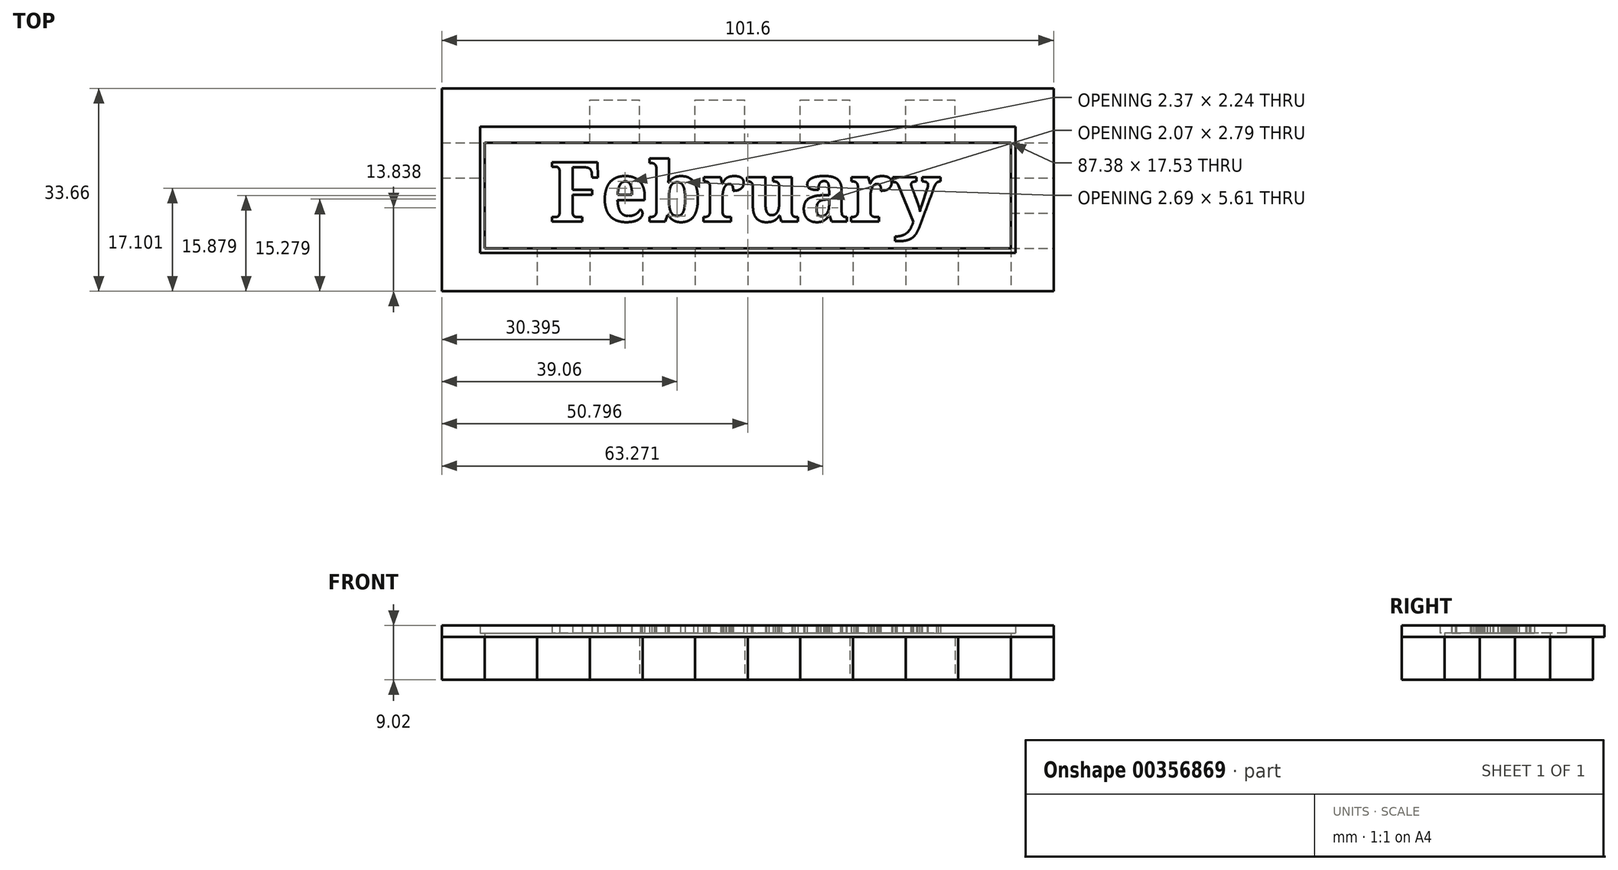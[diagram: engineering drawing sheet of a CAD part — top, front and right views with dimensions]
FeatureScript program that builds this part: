
annotation { "Feature Type Name" : "Feature", "Feature Type Description" : "" }
export const myFeature = defineFeature(function(context is Context, id is Id, definition is map)
    precondition{}
    {
        {
            var Q0;
            Q0=qCreatedBy(makeId("Top.planeOp"),FACE);
            var sketch = newSketch(context, id + "F0", { "sketchPlane" : qUnion([Q0])});
            skLineSegment(sketch, "E0.bottom", {"start": v(-52.12, 11.37) * mm, "end": v(49.48, 11.37) * mm});
            skLineSegment(sketch, "E0.top", {"start": v(-52.12, -20.38) * mm, "end": v(49.48, -20.38) * mm});
            skLineSegment(sketch, "E0.left", {"start": v(-52.12, 11.37) * mm, "end": v(-52.12, -20.38) * mm});
            skLineSegment(sketch, "E0.right", {"start": v(49.48, 11.37) * mm, "end": v(49.48, -20.38) * mm});
            skLineSegment(sketch, "E1.bottom", {"start": v(-52.12, 11.37) * mm, "end": v(-45.01, 11.37) * mm});
            skLineSegment(sketch, "E1.top", {"start": v(-52.12, 4.26) * mm, "end": v(-45.01, 4.26) * mm});
            skLineSegment(sketch, "E1.left", {"start": v(-52.12, 11.37) * mm, "end": v(-52.12, 4.26) * mm});
            skLineSegment(sketch, "E1.right", {"start": v(-45.01, 11.37) * mm, "end": v(-45.01, 4.26) * mm});
            skLineSegment(sketch, "E2.bottom", {"start": v(-45.01, 11.37) * mm, "end": v(-36.78, 11.37) * mm});
            skLineSegment(sketch, "E2.top", {"start": v(-45.01, 4.26) * mm, "end": v(-36.78, 4.26) * mm});
            skLineSegment(sketch, "E2.right", {"start": v(-36.78, 11.37) * mm, "end": v(-36.78, 4.26) * mm});
            skLineSegment(sketch, "E3.bottom", {"start": v(-36.78, 4.26) * mm, "end": v(-27.54, 4.26) * mm});
            skLineSegment(sketch, "E3.top", {"start": v(-36.78, 11.37) * mm, "end": v(-27.54, 11.37) * mm});
            skLineSegment(sketch, "E3.left", {"start": v(-36.78, 4.26) * mm, "end": v(-36.78, 11.37) * mm});
            skLineSegment(sketch, "E3.right", {"start": v(-27.54, 4.26) * mm, "end": v(-27.54, 11.37) * mm});
            skLineSegment(sketch, "E4.bottom", {"start": v(-27.54, 4.26) * mm, "end": v(-19.3, 4.26) * mm});
            skLineSegment(sketch, "E4.top", {"start": v(-27.54, 11.37) * mm, "end": v(-19.3, 11.37) * mm});
            skLineSegment(sketch, "E4.right", {"start": v(-19.3, 4.26) * mm, "end": v(-19.3, 11.37) * mm});
            skLineSegment(sketch, "E5.bottom", {"start": v(-19.3, 4.26) * mm, "end": v(-10.06, 4.26) * mm});
            skLineSegment(sketch, "E5.top", {"start": v(-19.3, 11.37) * mm, "end": v(-10.06, 11.37) * mm});
            skLineSegment(sketch, "E5.right", {"start": v(-10.06, 4.26) * mm, "end": v(-10.06, 11.37) * mm});
            skLineSegment(sketch, "E6.bottom", {"start": v(-10.06, 4.26) * mm, "end": v(-10.06, 4.26) * mm});
            skLineSegment(sketch, "E6.top", {"start": v(-10.06, 11.37) * mm, "end": v(-10.06, 11.37) * mm});
            skLineSegment(sketch, "E7.bottom", {"start": v(-10.06, 4.26) * mm, "end": v(-1.83, 4.26) * mm});
            skLineSegment(sketch, "E7.top", {"start": v(-10.06, 11.37) * mm, "end": v(-1.83, 11.37) * mm});
            skLineSegment(sketch, "E7.right", {"start": v(-1.83, 4.26) * mm, "end": v(-1.83, 11.37) * mm});
            skLineSegment(sketch, "E8.bottom", {"start": v(-1.83, 4.26) * mm, "end": v(7.41, 4.26) * mm});
            skLineSegment(sketch, "E8.top", {"start": v(-1.83, 11.37) * mm, "end": v(7.41, 11.37) * mm});
            skLineSegment(sketch, "E8.right", {"start": v(7.41, 4.26) * mm, "end": v(7.41, 11.37) * mm});
            skLineSegment(sketch, "E9.bottom", {"start": v(7.41, 4.26) * mm, "end": v(15.64, 4.26) * mm});
            skLineSegment(sketch, "E9.top", {"start": v(7.41, 11.37) * mm, "end": v(15.64, 11.37) * mm});
            skLineSegment(sketch, "E9.right", {"start": v(15.64, 4.26) * mm, "end": v(15.64, 11.37) * mm});
            skLineSegment(sketch, "E10.bottom", {"start": v(15.64, 4.26) * mm, "end": v(24.89, 4.26) * mm});
            skLineSegment(sketch, "E10.top", {"start": v(15.64, 11.37) * mm, "end": v(24.89, 11.37) * mm});
            skLineSegment(sketch, "E10.right", {"start": v(24.89, 4.26) * mm, "end": v(24.89, 11.37) * mm});
            skLineSegment(sketch, "E11.bottom", {"start": v(24.89, 4.26) * mm, "end": v(24.89, 4.26) * mm});
            skLineSegment(sketch, "E11.top", {"start": v(24.89, 11.37) * mm, "end": v(24.89, 11.37) * mm});
            skLineSegment(sketch, "E12.bottom", {"start": v(24.89, 4.26) * mm, "end": v(33.12, 4.26) * mm});
            skLineSegment(sketch, "E12.top", {"start": v(24.89, 11.37) * mm, "end": v(33.12, 11.37) * mm});
            skLineSegment(sketch, "E12.right", {"start": v(33.12, 4.26) * mm, "end": v(33.12, 11.37) * mm});
            skLineSegment(sketch, "E13.bottom", {"start": v(33.12, 4.26) * mm, "end": v(42.36, 4.26) * mm});
            skLineSegment(sketch, "E13.top", {"start": v(33.12, 11.37) * mm, "end": v(42.36, 11.37) * mm});
            skLineSegment(sketch, "E13.right", {"start": v(42.36, 4.26) * mm, "end": v(42.36, 11.37) * mm});
            skLineSegment(sketch, "E14.bottom", {"start": v(42.36, 4.26) * mm, "end": v(49.48, 4.26) * mm});
            skLineSegment(sketch, "E14.top", {"start": v(42.36, 11.37) * mm, "end": v(49.48, 11.37) * mm});
            skLineSegment(sketch, "E14.right", {"start": v(49.48, 4.26) * mm, "end": v(49.48, 11.37) * mm});
            skLineSegment(sketch, "E15.bottom", {"start": v(-52.12, -20.38) * mm, "end": v(-45.01, -20.38) * mm});
            skLineSegment(sketch, "E15.top", {"start": v(-52.12, -13.26) * mm, "end": v(-45.01, -13.26) * mm});
            skLineSegment(sketch, "E15.left", {"start": v(-52.12, -20.38) * mm, "end": v(-52.12, -13.26) * mm});
            skLineSegment(sketch, "E15.right", {"start": v(-45.01, -20.38) * mm, "end": v(-45.01, -13.26) * mm});
            skLineSegment(sketch, "E16.bottom", {"start": v(-45.01, -13.26) * mm, "end": v(-45.01, -13.26) * mm});
            skLineSegment(sketch, "E16.top", {"start": v(-45.01, -20.38) * mm, "end": v(-45.01, -20.38) * mm});
            skLineSegment(sketch, "E16.left", {"start": v(-45.01, -13.26) * mm, "end": v(-45.01, -20.38) * mm});
            skLineSegment(sketch, "E16.right", {"start": v(-45.01, -13.26) * mm, "end": v(-45.01, -20.38) * mm});
            skLineSegment(sketch, "E17.bottom", {"start": v(-45.01, -13.26) * mm, "end": v(-36.27, -13.26) * mm});
            skLineSegment(sketch, "E17.top", {"start": v(-45.01, -20.38) * mm, "end": v(-36.27, -20.38) * mm});
            skLineSegment(sketch, "E17.right", {"start": v(-36.27, -13.26) * mm, "end": v(-36.27, -20.38) * mm});
            skLineSegment(sketch, "E18.bottom", {"start": v(-36.27, -13.26) * mm, "end": v(-36.27, -13.26) * mm});
            skLineSegment(sketch, "E18.top", {"start": v(-36.27, -20.38) * mm, "end": v(-36.27, -20.38) * mm});
            skLineSegment(sketch, "E19.bottom", {"start": v(-36.27, -13.26) * mm, "end": v(-27.54, -13.26) * mm});
            skLineSegment(sketch, "E19.top", {"start": v(-36.27, -20.38) * mm, "end": v(-27.54, -20.38) * mm});
            skLineSegment(sketch, "E19.right", {"start": v(-27.54, -13.26) * mm, "end": v(-27.54, -20.38) * mm});
            skLineSegment(sketch, "E20.bottom", {"start": v(-27.54, -13.26) * mm, "end": v(-18.8, -13.26) * mm});
            skLineSegment(sketch, "E20.top", {"start": v(-27.54, -20.38) * mm, "end": v(-18.8, -20.38) * mm});
            skLineSegment(sketch, "E20.right", {"start": v(-18.8, -13.26) * mm, "end": v(-18.8, -20.38) * mm});
            skLineSegment(sketch, "E21.bottom", {"start": v(-18.8, -13.26) * mm, "end": v(-10.06, -13.26) * mm});
            skLineSegment(sketch, "E21.top", {"start": v(-18.8, -20.38) * mm, "end": v(-10.06, -20.38) * mm});
            skLineSegment(sketch, "E21.right", {"start": v(-10.06, -13.26) * mm, "end": v(-10.06, -20.38) * mm});
            skLineSegment(sketch, "E22.bottom", {"start": v(-10.06, -13.26) * mm, "end": v(-1.32, -13.26) * mm});
            skLineSegment(sketch, "E22.top", {"start": v(-10.06, -20.38) * mm, "end": v(-1.32, -20.38) * mm});
            skLineSegment(sketch, "E22.right", {"start": v(-1.32, -13.26) * mm, "end": v(-1.32, -20.38) * mm});
            skLineSegment(sketch, "E23.bottom", {"start": v(-1.32, -13.26) * mm, "end": v(7.41, -13.26) * mm});
            skLineSegment(sketch, "E23.top", {"start": v(-1.32, -20.38) * mm, "end": v(7.41, -20.38) * mm});
            skLineSegment(sketch, "E23.right", {"start": v(7.41, -13.26) * mm, "end": v(7.41, -20.38) * mm});
            skLineSegment(sketch, "E24.bottom", {"start": v(7.41, -13.26) * mm, "end": v(16.15, -13.26) * mm});
            skLineSegment(sketch, "E24.top", {"start": v(7.41, -20.38) * mm, "end": v(16.15, -20.38) * mm});
            skLineSegment(sketch, "E24.right", {"start": v(16.15, -13.26) * mm, "end": v(16.15, -20.38) * mm});
            skLineSegment(sketch, "E25.bottom", {"start": v(16.15, -13.26) * mm, "end": v(24.89, -13.26) * mm});
            skLineSegment(sketch, "E25.top", {"start": v(16.15, -20.38) * mm, "end": v(24.89, -20.38) * mm});
            skLineSegment(sketch, "E25.right", {"start": v(24.89, -13.26) * mm, "end": v(24.89, -20.38) * mm});
            skLineSegment(sketch, "E26.bottom", {"start": v(24.89, -13.26) * mm, "end": v(33.63, -13.26) * mm});
            skLineSegment(sketch, "E26.top", {"start": v(24.89, -20.38) * mm, "end": v(33.63, -20.38) * mm});
            skLineSegment(sketch, "E26.right", {"start": v(33.63, -13.26) * mm, "end": v(33.63, -20.38) * mm});
            skLineSegment(sketch, "E27.bottom", {"start": v(33.63, -13.26) * mm, "end": v(42.36, -13.26) * mm});
            skLineSegment(sketch, "E27.top", {"start": v(33.63, -20.38) * mm, "end": v(42.36, -20.38) * mm});
            skLineSegment(sketch, "E27.right", {"start": v(42.36, -13.26) * mm, "end": v(42.36, -20.38) * mm});
            skLineSegment(sketch, "E28.bottom", {"start": v(42.36, -13.26) * mm, "end": v(49.48, -13.26) * mm});
            skLineSegment(sketch, "E28.top", {"start": v(42.36, -20.38) * mm, "end": v(49.48, -20.38) * mm});
            skLineSegment(sketch, "E28.right", {"start": v(49.48, -13.26) * mm, "end": v(49.48, -20.38) * mm});
            skLineSegment(sketch, "E29.top", {"start": v(-52.12, -1.58) * mm, "end": v(-45.01, -1.58) * mm});
            skLineSegment(sketch, "E29.left", {"start": v(-52.12, 4.26) * mm, "end": v(-52.12, -1.58) * mm});
            skLineSegment(sketch, "E29.right", {"start": v(-45.01, 4.26) * mm, "end": v(-45.01, -1.58) * mm});
            skLineSegment(sketch, "E30.top", {"start": v(-52.12, -7.42) * mm, "end": v(-45.01, -7.42) * mm});
            skLineSegment(sketch, "E30.left", {"start": v(-52.12, -1.58) * mm, "end": v(-52.12, -7.42) * mm});
            skLineSegment(sketch, "E30.right", {"start": v(-45.01, -1.58) * mm, "end": v(-45.01, -7.42) * mm});
            skLineSegment(sketch, "E31.bottom", {"start": v(-45.01, -7.42) * mm, "end": v(-52.12, -7.42) * mm});
            skLineSegment(sketch, "E31.top", {"start": v(-45.01, -13.26) * mm, "end": v(-52.12, -13.26) * mm});
            skLineSegment(sketch, "E31.left", {"start": v(-45.01, -7.42) * mm, "end": v(-45.01, -13.26) * mm});
            skLineSegment(sketch, "E31.right", {"start": v(-52.12, -7.42) * mm, "end": v(-52.12, -13.26) * mm});
            skLineSegment(sketch, "E32.top", {"start": v(42.36, -1.58) * mm, "end": v(49.48, -1.58) * mm});
            skLineSegment(sketch, "E32.left", {"start": v(42.36, 4.26) * mm, "end": v(42.36, -1.58) * mm});
            skLineSegment(sketch, "E32.right", {"start": v(49.48, 4.26) * mm, "end": v(49.48, -1.58) * mm});
            skLineSegment(sketch, "E33.top", {"start": v(42.36, -7.42) * mm, "end": v(49.48, -7.42) * mm});
            skLineSegment(sketch, "E33.left", {"start": v(42.36, -1.58) * mm, "end": v(42.36, -7.42) * mm});
            skLineSegment(sketch, "E33.right", {"start": v(49.48, -1.58) * mm, "end": v(49.48, -7.42) * mm});
            skLineSegment(sketch, "E34.left", {"start": v(42.36, -7.42) * mm, "end": v(42.36, -13.26) * mm});
            skLineSegment(sketch, "E34.right", {"start": v(49.48, -7.42) * mm, "end": v(49.48, -13.26) * mm});
            skSolve(sketch);
        }
        {
            var Q0;
            Q0=makeQuery(id+"F0.imprint","IMPRINT",FACE,{"disambiguationData":[TD([[makeQuery(id+"F0.imprint","IMPRINT",EDGE,{"derivedFrom":sQuery(id+"F0.wireOp",EDGE,"E2.top")}),-1.0]])]});
            var Q1;
            Q1=makeQuery(id+"F0.imprint","IMPRINT",FACE,{"disambiguationData":[TD([[makeQuery(id+"F0.imprint","IMPRINT",EDGE,{"derivedFrom":sQuery(id+"F0.wireOp",EDGE,"E2.bottom")}),-1.0]])]});
            var Q2;
            Q2=makeQuery(id+"F0.imprint","IMPRINT",FACE,{"disambiguationData":[TD([[makeQuery(id+"F0.imprint","IMPRINT",EDGE,{"derivedFrom":sQuery(id+"F0.wireOp",EDGE,"E4.bottom")}),1.0]])]});
            var Q3;
            Q3=makeQuery(id+"F0.imprint","IMPRINT",FACE,{"disambiguationData":[TD([[makeQuery(id+"F0.imprint","IMPRINT",EDGE,{"derivedFrom":sQuery(id+"F0.wireOp",EDGE,"E7.bottom")}),1.0]])]});
            var Q4;
            Q4=makeQuery(id+"F0.imprint","IMPRINT",FACE,{"disambiguationData":[TD([[makeQuery(id+"F0.imprint","IMPRINT",EDGE,{"derivedFrom":sQuery(id+"F0.wireOp",EDGE,"E9.bottom")}),1.0]])]});
            var Q5;
            Q5=makeQuery(id+"F0.imprint","IMPRINT",FACE,{"disambiguationData":[TD([[makeQuery(id+"F0.imprint","IMPRINT",EDGE,{"derivedFrom":sQuery(id+"F0.wireOp",EDGE,"E12.bottom")}),1.0]])]});
            var Q6;
            Q6=makeQuery(id+"F0.imprint","IMPRINT",FACE,{"disambiguationData":[TD([[makeQuery(id+"F0.imprint","IMPRINT",EDGE,{"derivedFrom":sQuery(id+"F0.wireOp",EDGE,"E14.bottom")}),-1.0]])]});
            var Q7;
            Q7=makeQuery(id+"F0.imprint","IMPRINT",FACE,{"disambiguationData":[TD([[makeQuery(id+"F0.imprint","IMPRINT",EDGE,{"derivedFrom":sQuery(id+"F0.wireOp",EDGE,"E33.top")}),-1.0]])]});
            var Q8;
            Q8=makeQuery(id+"F0.imprint","IMPRINT",FACE,{"disambiguationData":[TD([[makeQuery(id+"F0.imprint","IMPRINT",EDGE,{"derivedFrom":sQuery(id+"F0.wireOp",EDGE,"E27.bottom")}),-1.0]])]});
            var Q9;
            Q9=makeQuery(id+"F0.imprint","IMPRINT",FACE,{"disambiguationData":[TD([[makeQuery(id+"F0.imprint","IMPRINT",EDGE,{"derivedFrom":sQuery(id+"F0.wireOp",EDGE,"E25.bottom")}),-1.0]])]});
            var Q10;
            Q10=makeQuery(id+"F0.imprint","IMPRINT",FACE,{"disambiguationData":[TD([[makeQuery(id+"F0.imprint","IMPRINT",EDGE,{"derivedFrom":sQuery(id+"F0.wireOp",EDGE,"E23.bottom")}),-1.0]])]});
            var Q11;
            Q11=makeQuery(id+"F0.imprint","IMPRINT",FACE,{"disambiguationData":[TD([[makeQuery(id+"F0.imprint","IMPRINT",EDGE,{"derivedFrom":sQuery(id+"F0.wireOp",EDGE,"E21.bottom")}),-1.0]])]});
            var Q12;
            Q12=makeQuery(id+"F0.imprint","IMPRINT",FACE,{"disambiguationData":[TD([[makeQuery(id+"F0.imprint","IMPRINT",EDGE,{"derivedFrom":sQuery(id+"F0.wireOp",EDGE,"E19.bottom")}),-1.0]])]});
            var Q13;
            Q13=makeQuery(id+"F0.imprint","IMPRINT",FACE,{"disambiguationData":[TD([[makeQuery(id+"F0.imprint","IMPRINT",EDGE,{"derivedFrom":sQuery(id+"F0.wireOp",EDGE,"E31.bottom")}),1.0]])]});
            var Q14;
            Q14=makeQuery(id+"F0.imprint","IMPRINT",FACE,{"disambiguationData":[TD([[makeQuery(id+"F0.imprint","IMPRINT",EDGE,{"derivedFrom":sQuery(id+"F0.wireOp",EDGE,"E1.top")}),-1.0]])]});
            extrude(context, id + "F1", {"entities" : qUnion([Q0, Q1, Q2, Q3, Q4, Q5, Q6, Q7, Q8, Q9, Q10, Q11, Q12, Q13, Q14]), "depth" : 7.11 * mm});
        }
        {
            var Q0;
            Q0=makeQuery(id+"F1.opExtrude","CAP_FACE",FACE,{"disambiguationData":[OSD([sQuery(id+"F0.wireOp",EDGE,"E2.bottom"),sQuery(id+"F0.wireOp",EDGE,"E1.right"),sQuery(id+"F0.wireOp",EDGE,"E3.bottom"),sQuery(id+"F0.wireOp",EDGE,"E3.left"),sQuery(id+"F0.wireOp",EDGE,"E4.top"),sQuery(id+"F0.wireOp",EDGE,"E3.right"),sQuery(id+"F0.wireOp",EDGE,"E5.bottom"),sQuery(id+"F0.wireOp",EDGE,"E4.right"),sQuery(id+"F0.wireOp",EDGE,"E6.top"),sQuery(id+"F0.wireOp",EDGE,"E5.right"),sQuery(id+"F0.wireOp",EDGE,"E7.bottom"),sQuery(id+"F0.wireOp",EDGE,"E5.right"),sQuery(id+"F0.wireOp",EDGE,"E8.top"),sQuery(id+"F0.wireOp",EDGE,"E7.right"),sQuery(id+"F0.wireOp",EDGE,"E9.bottom"),sQuery(id+"F0.wireOp",EDGE,"E8.right"),sQuery(id+"F0.wireOp",EDGE,"E10.top"),sQuery(id+"F0.wireOp",EDGE,"E9.right"),sQuery(id+"F0.wireOp",EDGE,"E11.bottom"),sQuery(id+"F0.wireOp",EDGE,"E10.right"),sQuery(id+"F0.wireOp",EDGE,"E12.top"),sQuery(id+"F0.wireOp",EDGE,"E10.right"),sQuery(id+"F0.wireOp",EDGE,"E13.bottom"),sQuery(id+"F0.wireOp",EDGE,"E12.right"),sQuery(id+"F0.wireOp",EDGE,"E16.bottom"),sQuery(id+"F0.wireOp",EDGE,"E17.top"),sQuery(id+"F0.wireOp",EDGE,"E16.left"),sQuery(id+"F0.wireOp",EDGE,"E18.bottom"),sQuery(id+"F0.wireOp",EDGE,"E17.right"),sQuery(id+"F0.wireOp",EDGE,"E19.top"),sQuery(id+"F0.wireOp",EDGE,"E17.right"),sQuery(id+"F0.wireOp",EDGE,"E20.bottom"),sQuery(id+"F0.wireOp",EDGE,"E19.right"),sQuery(id+"F0.wireOp",EDGE,"E21.top"),sQuery(id+"F0.wireOp",EDGE,"E20.right"),sQuery(id+"F0.wireOp",EDGE,"E22.bottom"),sQuery(id+"F0.wireOp",EDGE,"E21.right"),sQuery(id+"F0.wireOp",EDGE,"E23.top"),sQuery(id+"F0.wireOp",EDGE,"E22.right"),sQuery(id+"F0.wireOp",EDGE,"E24.bottom"),sQuery(id+"F0.wireOp",EDGE,"E23.right"),sQuery(id+"F0.wireOp",EDGE,"E25.top"),sQuery(id+"F0.wireOp",EDGE,"E24.right"),sQuery(id+"F0.wireOp",EDGE,"E26.bottom"),sQuery(id+"F0.wireOp",EDGE,"E25.right"),sQuery(id+"F0.wireOp",EDGE,"E27.top"),sQuery(id+"F0.wireOp",EDGE,"E26.right"),sQuery(id+"F0.wireOp",EDGE,"E27.right"),sQuery(id+"F0.wireOp",EDGE,"E1.top"),sQuery(id+"F0.wireOp",EDGE,"E29.left"),sQuery(id+"F0.wireOp",EDGE,"E29.top"),sQuery(id+"F0.wireOp",EDGE,"E30.right"),sQuery(id+"F0.wireOp",EDGE,"E31.bottom"),sQuery(id+"F0.wireOp",EDGE,"E31.top"),sQuery(id+"F0.wireOp",EDGE,"E31.right"),sQuery(id+"F0.wireOp",EDGE,"E14.bottom"),sQuery(id+"F0.wireOp",EDGE,"E32.right"),sQuery(id+"F0.wireOp",EDGE,"E32.top"),sQuery(id+"F0.wireOp",EDGE,"E33.left"),sQuery(id+"F0.wireOp",EDGE,"E33.top"),sQuery(id+"F0.wireOp",EDGE,"E28.bottom"),sQuery(id+"F0.wireOp",EDGE,"E34.right")])],"isStart":false});
            var sketch = newSketch(context, id + "F2", { "sketchPlane" : qUnion([Q0])});
            skLineSegment(sketch, "E35.bottom", {"start": v(-52.12, -20.38) * mm, "end": v(-45.01, -20.38) * mm});
            skLineSegment(sketch, "E35.top", {"start": v(-52.12, 13.28) * mm, "end": v(-45.01, 13.28) * mm});
            skLineSegment(sketch, "E35.left", {"start": v(-52.12, -20.38) * mm, "end": v(-52.12, 13.28) * mm});
            skLineSegment(sketch, "E35.right", {"start": v(-45.01, -20.38) * mm, "end": v(-45.01, 13.28) * mm});
            skLineSegment(sketch, "E36.bottom", {"start": v(-52.12, -20.38) * mm, "end": v(49.48, -20.38) * mm});
            skLineSegment(sketch, "E36.top", {"start": v(-52.12, -13.26) * mm, "end": v(49.48, -13.26) * mm});
            skLineSegment(sketch, "E36.left", {"start": v(-52.12, -20.38) * mm, "end": v(-52.12, -13.26) * mm});
            skLineSegment(sketch, "E36.right", {"start": v(49.48, -20.38) * mm, "end": v(49.48, -13.26) * mm});
            skPoint(sketch, "E37.oppositeSnap0", {"position": v(42.36, -4.5) * mm});
            skLineSegment(sketch, "E37.bottom", {"start": v(49.48, -20.38) * mm, "end": v(42.36, -20.38) * mm});
            skLineSegment(sketch, "E37.top", {"start": v(49.48, 13.28) * mm, "end": v(42.36, 13.28) * mm});
            skLineSegment(sketch, "E37.left", {"start": v(49.48, -20.38) * mm, "end": v(49.48, 13.28) * mm});
            skLineSegment(sketch, "E37.right", {"start": v(42.36, -20.38) * mm, "end": v(42.36, 13.28) * mm});
            skLineSegment(sketch, "E38.bottom", {"start": v(-52.12, 13.28) * mm, "end": v(49.48, 13.28) * mm});
            skLineSegment(sketch, "E38.top", {"start": v(-52.12, 4.26) * mm, "end": v(49.48, 4.26) * mm});
            skLineSegment(sketch, "E38.left", {"start": v(-52.12, 13.28) * mm, "end": v(-52.12, 4.26) * mm});
            skLineSegment(sketch, "E38.right", {"start": v(49.48, 13.28) * mm, "end": v(49.48, 4.26) * mm});
            skSolve(sketch);
        }
        {
            var Q0;
            Q0=qSketchRegion(id+"F2",true);
            var Q1;
            {var subQ5=sQuery(id+"F2.wireOp",EDGE,"E36.top");var subQ10=sQuery(id+"F2.wireOp",EDGE,"E35.right");var subQ12=makeQuery(id+"F2.imprint","INTERSECT",VERTEX,{"derivedFrom":[makeQuery(id+"F1.opExtrude","CAP_EDGE",EDGE,{"disambiguationData":[OSD([sQuery(id+"F0.wireOp",EDGE,"E31.bottom")])],"isStart":false}),subQ10]});var subQ24=makeQuery(id+"F2.imprint","INTERSECT",VERTEX,{"derivedFrom":[subQ10,subQ5]});Q1=makeQuery(id+"F2.imprint","IMPRINT",FACE,{"disambiguationData":[TD([[makeQuery(id+"F2.imprint","IMPRINT",EDGE,{"disambiguationData":[TD([[subQ12,1.0],[subQ24,-1.0]])],"derivedFrom":subQ10}),-1.0]])]});}
            extrude(context, id + "F3", {"entities" : qUnion([Q0, Q1]), "depth" : 0.64 * mm});
        }
        {
            var Q0;
            Q0=makeQuery(id+"F3.opExtrude","CAP_FACE",FACE,{"disambiguationData":[OSD([sQuery(id+"F2.wireOp",EDGE,"E35.left"),sQuery(id+"F2.wireOp",EDGE,"E36.bottom"),sQuery(id+"F2.wireOp",EDGE,"E36.left"),sQuery(id+"F2.wireOp",EDGE,"E37.bottom"),sQuery(id+"F2.wireOp",EDGE,"E37.left"),sQuery(id+"F2.wireOp",EDGE,"E38.bottom"),sQuery(id+"F2.wireOp",EDGE,"E38.left"),sQuery(id+"F2.wireOp",EDGE,"E38.right")])],"isStart":false});
            var sketch = newSketch(context, id + "F4", { "sketchPlane" : qUnion([Q0])});
            skLineSegment(sketch, "E39.bottom", {"start": v(-52.12, 13.28) * mm, "end": v(49.48, 13.28) * mm});
            skLineSegment(sketch, "E39.top", {"start": v(-52.12, 6.93) * mm, "end": v(49.48, 6.93) * mm});
            skLineSegment(sketch, "E39.left", {"start": v(-52.12, 13.28) * mm, "end": v(-52.12, 6.93) * mm});
            skLineSegment(sketch, "E39.right", {"start": v(49.48, 13.28) * mm, "end": v(49.48, 6.93) * mm});
            skLineSegment(sketch, "E40.bottom", {"start": v(-52.12, 13.28) * mm, "end": v(-45.77, 13.28) * mm});
            skLineSegment(sketch, "E40.top", {"start": v(-52.12, -20.38) * mm, "end": v(-45.77, -20.38) * mm});
            skLineSegment(sketch, "E40.left", {"start": v(-52.12, 13.28) * mm, "end": v(-52.12, -20.38) * mm});
            skLineSegment(sketch, "E40.right", {"start": v(-45.77, 13.28) * mm, "end": v(-45.77, -20.38) * mm});
            skLineSegment(sketch, "E41.bottom", {"start": v(-52.12, -14.03) * mm, "end": v(49.48, -14.03) * mm});
            skLineSegment(sketch, "E41.top", {"start": v(-52.12, -20.38) * mm, "end": v(49.48, -20.38) * mm});
            skLineSegment(sketch, "E41.left", {"start": v(-52.12, -14.03) * mm, "end": v(-52.12, -20.38) * mm});
            skLineSegment(sketch, "E41.right", {"start": v(49.48, -14.03) * mm, "end": v(49.48, -20.38) * mm});
            skLineSegment(sketch, "E42.bottom", {"start": v(49.48, -20.38) * mm, "end": v(43.13, -20.38) * mm});
            skLineSegment(sketch, "E42.top", {"start": v(49.48, 13.28) * mm, "end": v(43.13, 13.28) * mm});
            skLineSegment(sketch, "E42.left", {"start": v(49.48, -20.38) * mm, "end": v(49.48, 13.28) * mm});
            skLineSegment(sketch, "E42.right", {"start": v(43.13, -20.38) * mm, "end": v(43.13, 13.28) * mm});
            skSolve(sketch);
        }
        {
            var Q0;
            Q0=qSketchRegion(id+"F4",true);
            extrude(context, id + "F5", {"entities" : qUnion([Q0]), "operationType" : NewBodyOperationType.ADD, "depth" : 1.27 * mm});
        }
        {
            var Q0;
            Q0=makeQuery(id+"F3.opExtrude","CAP_FACE",FACE,{"disambiguationData":[OSD([sQuery(id+"F2.wireOp",EDGE,"E35.left"),sQuery(id+"F2.wireOp",EDGE,"E36.bottom"),sQuery(id+"F2.wireOp",EDGE,"E36.left"),sQuery(id+"F2.wireOp",EDGE,"E37.bottom"),sQuery(id+"F2.wireOp",EDGE,"E37.left"),sQuery(id+"F2.wireOp",EDGE,"E38.bottom"),sQuery(id+"F2.wireOp",EDGE,"E38.left"),sQuery(id+"F2.wireOp",EDGE,"E38.right")])],"isStart":false});
            var sketch = newSketch(context, id + "F6", { "sketchPlane" : qUnion([Q0])});
            skText(sketch, "E43", { "text": "February", "fontName": "NotoSerif-Bold.ttf"});
            const initialGuessF6  = {"E43": [-0.03422, -0.0088, 1, 0, 0.00988]};
            skSetInitialGuess(sketch, initialGuessF6);
            skSolve(sketch);
        }
        {
            var Q0;
            Q0 = qSketchRegion(id + "F6", true);
            extrude(context, id + "F7", {"entities" : qUnion([Q0]), "operationType" : NewBodyOperationType.ADD, "depth" : 1.27 * mm});
        }
    });
